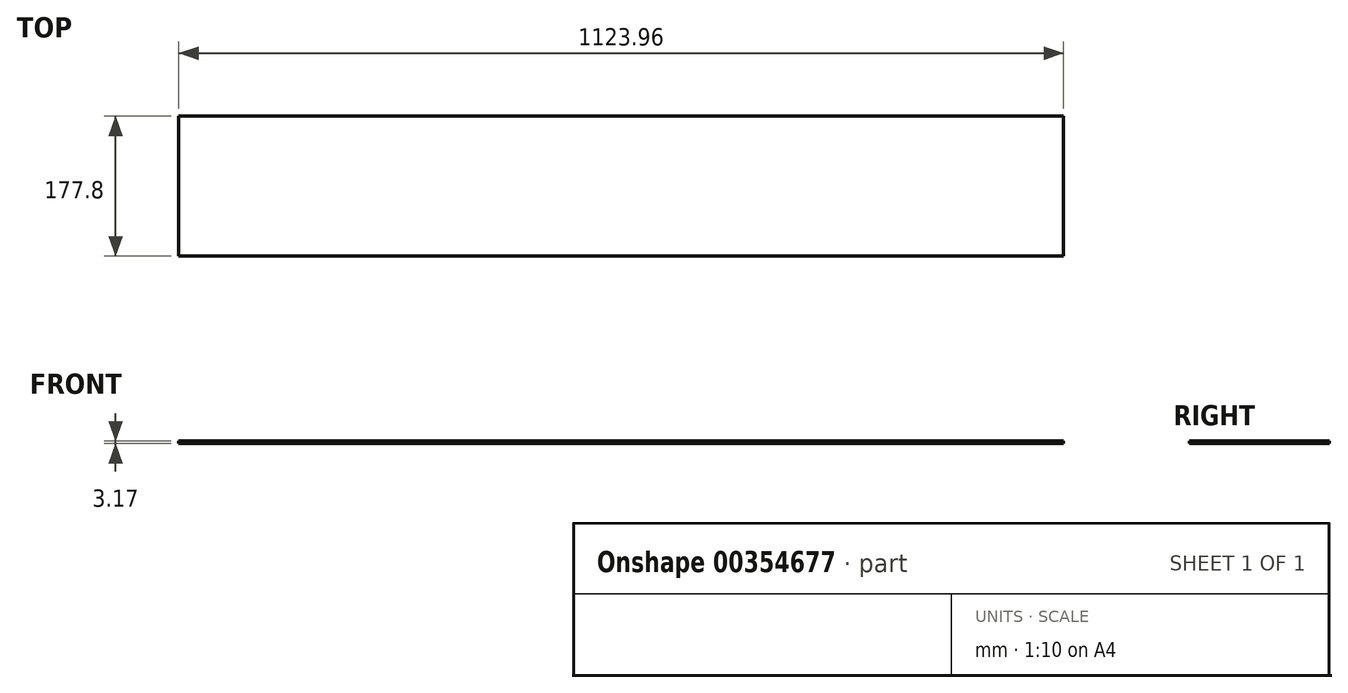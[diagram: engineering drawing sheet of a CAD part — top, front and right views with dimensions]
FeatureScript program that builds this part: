
annotation { "Feature Type Name" : "Feature", "Feature Type Description" : "" }
export const myFeature = defineFeature(function(context is Context, id is Id, definition is map)
    precondition{}
    {
        {
            var Q0;
            Q0=qCreatedBy(makeId("Top.planeOp"),FACE);
            var sketch = newSketch(context, id + "F0", { "sketchPlane" : qUnion([Q0])});
            skLineSegment(sketch, "E0.bottom", {"start": v(-561.98, 88.9) * mm, "end": v(561.98, 88.9) * mm});
            skLineSegment(sketch, "E0.top", {"start": v(-561.98, -88.9) * mm, "end": v(561.98, -88.9) * mm});
            skLineSegment(sketch, "E0.left", {"start": v(-561.98, 88.9) * mm, "end": v(-561.98, -88.9) * mm});
            skLineSegment(sketch, "E0.right", {"start": v(561.98, 88.9) * mm, "end": v(561.98, -88.9) * mm});
            skPoint(sketch, "E0.middle", {"position": v(0, 0) * mm});
            skSolve(sketch);
        }
        {
            var Q0;
            Q0=qSketchRegion(id+"F0",true);
            extrude(context, id + "F1", {"entities" : qUnion([Q0]), "depth" : 3.17 * mm});
        }
    });
